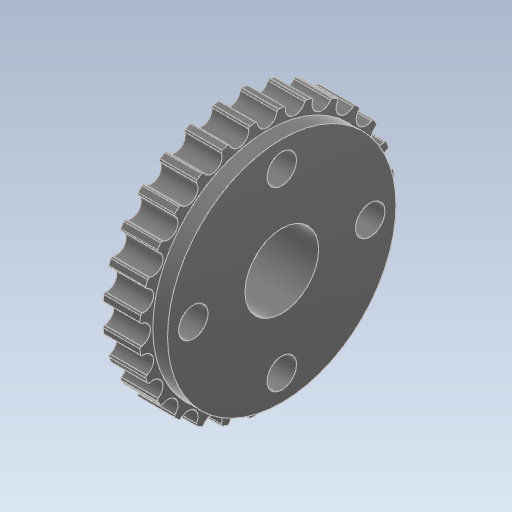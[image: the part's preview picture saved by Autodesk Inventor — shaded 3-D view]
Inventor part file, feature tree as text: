
AUTODESK INVENTOR PART (.ipt)
format: ipt  version: 2024 (Build 280153000, 153)  size: 401,920 bytes
history: native  units: mm
features: other x3, sketch x2, revolve x1, extrude x1
ambient origin geometry x8: Origin, YZ Plane, XZ Plane, XY Plane, X Axis, Y Axis, Z Axis, Center Point
bodies: Solid1_1 (feature_tree)
feature tree (7):
  other  "_GPA28GT2040-A-H5.ipt"
  revolve  "回転1"
  extrude  "押し出し2"  TaperAngle=360.0deg  [1 undecoded]
  sketch  "スケッチ2"
  other  "Solid1::_GPA28GT2040-A-H5.ipt"
  other  "TaggingFeature2"
  sketch  "スケッチ4"
note: 1 required parameter value undecoded (feature->parameter linkage not recoverable at this tier; creation-order binding heuristic only, values carry confidence <= 0.55)
